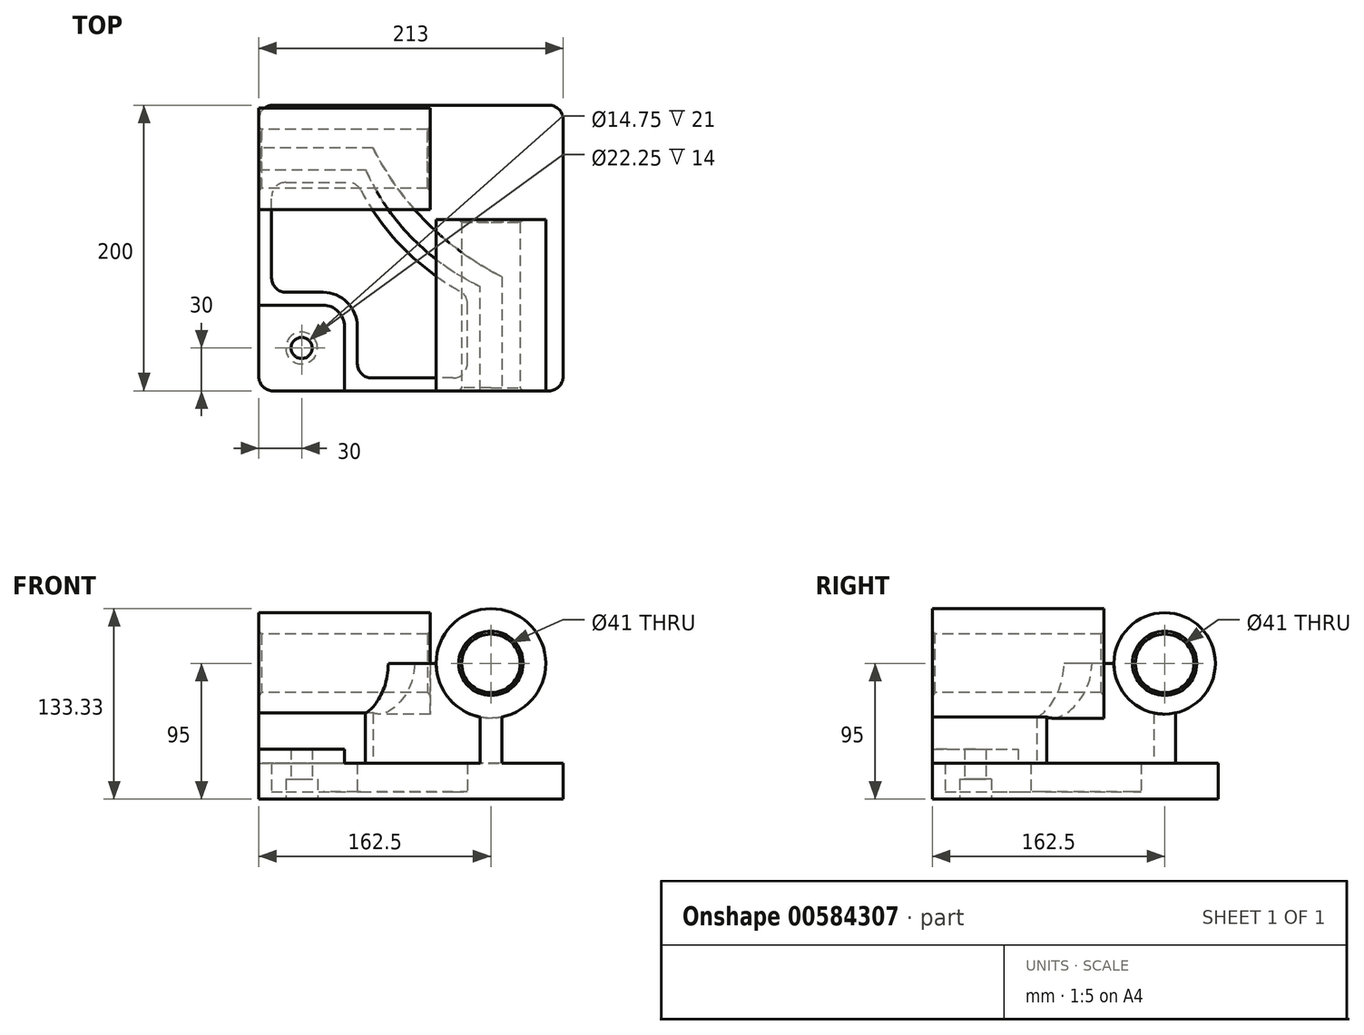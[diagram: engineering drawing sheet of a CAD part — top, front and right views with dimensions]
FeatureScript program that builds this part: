
annotation { "Feature Type Name" : "Feature", "Feature Type Description" : "" }
export const myFeature = defineFeature(function(context is Context, id is Id, definition is map)
    precondition{}
    {
        {
            var Q0;
            Q0=qCreatedBy(makeId("Top.planeOp"),FACE);
            var sketch = newSketch(context, id + "F0", { "sketchPlane" : qUnion([Q0])});
            skLineSegment(sketch, "E0", {"start": v(-96.5, 0) * mm, "end": v(96.5, 0) * mm});
            skLineSegment(sketch, "E1", {"start": v(106.5, 10) * mm, "end": v(106.5, 190) * mm});
            skLineSegment(sketch, "E2", {"start": v(96.5, 200) * mm, "end": v(-96.5, 200) * mm});
            skLineSegment(sketch, "E3", {"start": v(-106.5, 10) * mm, "end": v(-106.5, 190) * mm});
            skLineSegment(sketch, "E4", {"start": v(0, 0) * mm, "end": v(0, 200) * mm, "construction": true});
            skLineSegment(sketch, "E5", {"start": v(106.5, 100) * mm, "end": v(-106.5, 100) * mm, "construction": true});
            skPoint(sketch, "E6", {"position": v(63.5, 0) * mm});
            skPoint(sketch, "E7", {"position": v(48.5, 0) * mm});
            skLineSegment(sketch, "E8", {"start": v(48.5, 0) * mm, "end": v(48.5, 9) * mm});
            skLineSegment(sketch, "E9", {"start": v(63.5, 0) * mm, "end": v(63.5, 80) * mm});
            skPoint(sketch, "E10.visualSharp", {"position": v(106.5, 200) * mm});
            skArc(sketch, "E10.filletArc", {"start": v(106.5, 190) * mm, "mid": v(103.57, 197.07) * mm, "end": v(96.5, 200) * mm});
            skPoint(sketch, "E11.visualSharp", {"position": v(-106.5, 200) * mm});
            skArc(sketch, "E11.filletArc", {"start": v(-96.5, 200) * mm, "mid": v(-103.57, 197.07) * mm, "end": v(-106.5, 190) * mm});
            skPoint(sketch, "E12.visualSharp", {"position": v(106.5, 0) * mm});
            skArc(sketch, "E12.filletArc", {"start": v(96.5, 0) * mm, "mid": v(103.57, 2.93) * mm, "end": v(106.5, 10) * mm});
            skPoint(sketch, "E13.visualSharp", {"position": v(-106.5, 0) * mm});
            skArc(sketch, "E13.filletArc", {"start": v(-106.5, 10) * mm, "mid": v(-103.57, 2.93) * mm, "end": v(-96.5, 0) * mm});
            skPoint(sketch, "E14", {"position": v(-106.5, 155) * mm});
            skPoint(sketch, "E15", {"position": v(-106.5, 170) * mm});
            skPoint(sketch, "E16", {"position": v(-97.5, 200) * mm});
            skLineSegment(sketch, "E17", {"start": v(-106.5, 170) * mm, "end": v(-26.5, 170) * mm});
            skLineSegment(sketch, "E18", {"start": v(-46.5, 0) * mm, "end": v(-46.5, 45) * mm});
            skLineSegment(sketch, "E19", {"start": v(-61.5, 60) * mm, "end": v(-106.5, 60) * mm});
            skPoint(sketch, "E20.visualSharp", {"position": v(-46.5, 60) * mm});
            skArc(sketch, "E20.filletArc", {"start": v(-46.5, 45) * mm, "mid": v(-50.9, 55.6) * mm, "end": v(-61.5, 60) * mm});
            skLineSegment(sketch, "E21", {"start": v(-87.5, 69) * mm, "end": v(-61.5, 69) * mm});
            skLineSegment(sketch, "E22", {"start": v(-37.5, 19) * mm, "end": v(-37.5, 45) * mm});
            skPoint(sketch, "E23.visualSharp", {"position": v(-37.5, 69) * mm});
            skArc(sketch, "E23.filletArc", {"start": v(-37.5, 45) * mm, "mid": v(-44.53, 61.97) * mm, "end": v(-61.5, 69) * mm});
            skLineSegment(sketch, "E24", {"start": v(-106.5, 155) * mm, "end": v(-31.82, 155) * mm});
            skLineSegment(sketch, "E25", {"start": v(-97.5, 79) * mm, "end": v(-97.5, 136) * mm});
            skLineSegment(sketch, "E26", {"start": v(-87.5, 146) * mm, "end": v(-44.04, 146) * mm});
            skPoint(sketch, "E27.visualSharp", {"position": v(-97.5, 69) * mm});
            skArc(sketch, "E27.filletArc", {"start": v(-97.5, 79) * mm, "mid": v(-94.57, 71.93) * mm, "end": v(-87.5, 69) * mm});
            skPoint(sketch, "E28.visualSharp", {"position": v(-97.5, 146) * mm});
            skArc(sketch, "E28.filletArc", {"start": v(-87.5, 146) * mm, "mid": v(-94.57, 143.07) * mm, "end": v(-97.5, 136) * mm});
            skLineSegment(sketch, "E29", {"start": v(29.5, 9) * mm, "end": v(-27.5, 9) * mm});
            skPoint(sketch, "E30.visualSharp", {"position": v(-37.5, 9) * mm});
            skArc(sketch, "E30.filletArc", {"start": v(-37.5, 19) * mm, "mid": v(-34.57, 11.93) * mm, "end": v(-27.5, 9) * mm});
            skArc(sketch, "E31", {"start": v(-26.5, 170) * mm, "mid": v(11.24, 117.74) * mm, "end": v(63.5, 80) * mm});
            skLineSegment(sketch, "E32", {"start": v(48.5, 9) * mm, "end": v(48.5, 73.06) * mm});
            skArc(sketch, "E33", {"start": v(-31.82, 155) * mm, "mid": v(1, 106.83) * mm, "end": v(48.5, 73.06) * mm});
            skPoint(sketch, "E34", {"position": v(39.5, 9) * mm});
            skLineSegment(sketch, "E35", {"start": v(39.5, 19) * mm, "end": v(39.5, 61.05) * mm});
            skArc(sketch, "E36", {"start": v(-35.2, 140.68) * mm, "mid": v(-5.58, 100.18) * mm, "end": v(34.35, 69.8) * mm});
            skPoint(sketch, "E37.visualSharp", {"position": v(-37.9, 146) * mm});
            skArc(sketch, "E37.filletArc", {"start": v(-35.2, 140.68) * mm, "mid": v(-38.88, 144.57) * mm, "end": v(-44.04, 146) * mm});
            skPoint(sketch, "E38.visualSharp", {"position": v(39.5, 67.06) * mm});
            skArc(sketch, "E38.filletArc", {"start": v(39.5, 61.05) * mm, "mid": v(38.12, 66.13) * mm, "end": v(34.35, 69.8) * mm});
            skArc(sketch, "E39.filletArc", {"start": v(29.5, 9) * mm, "mid": v(36.57, 11.93) * mm, "end": v(39.5, 19) * mm});
            skLineSegment(sketch, "E40", {"start": v(-76.5, 0) * mm, "end": v(-76.5, 60) * mm, "construction": true});
            skLineSegment(sketch, "E41", {"start": v(-106.5, 30) * mm, "end": v(-46.5, 30) * mm, "construction": true});
            skPoint(sketch, "E42.center.orphan", {"position": v(-76.5, 30) * mm});
            skSolve(sketch);
        }
        {
            var Q0;
            {var subQ1=sQuery(id+"F0.wireOp",EDGE,"E13.filletArc");Q0=makeQuery(id+"F0.imprint","IMPRINT",FACE,{"disambiguationData":[TD([[makeQuery(id+"F0.imprint","IMPRINT",EDGE,{"derivedFrom":subQ1}),1.0]])]});}
            extrude(context, id + "F1", {"entities" : qUnion([Q0]), "depth" : 35 * mm, "offsetDistance" : 25 * mm});
        }
        {
            var Q0;
            {var subQ0=sQuery(id+"F0.wireOp",EDGE,"E8");Q0=makeQuery(id+"F0.imprint","IMPRINT",FACE,{"disambiguationData":[TD([[makeQuery(id+"F0.imprint","IMPRINT",EDGE,{"derivedFrom":subQ0}),1.0]])]});}
            extrude(context, id + "F2", {"entities" : qUnion([Q0]), "operationType" : NewBodyOperationType.ADD, "depth" : 25 * mm, "offsetDistance" : 25 * mm});
        }
        {
            var Q0;
            Q0=makeQuery(id+"F0.imprint","IMPRINT",FACE,{"disambiguationData":[TD([[makeQuery(id+"F0.imprint","IMPRINT",EDGE,{"derivedFrom":sQuery(id+"F0.wireOp",EDGE,"E21")}),1.0]])]});
            extrude(context, id + "F3", {"entities" : qUnion([Q0]), "operationType" : NewBodyOperationType.ADD, "depth" : 5 * mm, "offsetDistance" : 25 * mm});
        }
        {
            var Q0;
            {var subQ1=sQuery(id+"F0.wireOp",EDGE,"E8");Q0=makeQuery(id+"F0.imprint","IMPRINT",FACE,{"disambiguationData":[TD([[makeQuery(id+"F0.imprint","IMPRINT",EDGE,{"derivedFrom":subQ1}),-1.0]])]});}
            extrude(context, id + "F4", {"entities" : qUnion([Q0]), "operationType" : NewBodyOperationType.ADD, "depth" : 95 * mm, "offsetDistance" : 25 * mm});
        }
        {
            var Q0;
            Q0=sQuery(id+"F0.wireOp",VERTEX,"E42.center.orphan");
            var Q1;
            Q1=makeQuery(id+"F1.opExtrude","SWEPT_BODY",BODY,{"disambiguationData":[OSD([sQuery(id+"F0.wireOp",EDGE,"E0"),sQuery(id+"F0.wireOp",EDGE,"E3"),sQuery(id+"F0.wireOp",EDGE,"E13.filletArc"),sQuery(id+"F0.wireOp",EDGE,"E18"),sQuery(id+"F0.wireOp",EDGE,"E19"),sQuery(id+"F0.wireOp",EDGE,"E20.filletArc")])]});
            hole(context, id + "F5", {"style" : HoleStyle.C_BORE, "endStyle" : HoleEndStyle.THROUGH, "oppositeDirection" : true, "standardTappedOrClearance" : lookupTablePath({ "standard" : "ISO", "fit" : "Close", "size" : "M14", "type" : "Clearance" }), "standardBlindInLast" : lookupTablePath({ "fit" : "Close", "standard" : "ISO", "size" : "M14", "type" : "Clearance" }), "holeDiameter" : 14.75 * mm, "cBoreDiameter" : 22.25 * mm, "cBoreDepth" : 14 * mm, "majorDiameter" : 5 * mm, "isTappedThrough" : true, "tappedDepth" : 12 * mm, "tapClearance" : 3, "locations" : qUnion([Q0]), "scope" : qUnion([Q1])});
        }
        {
            var Q0;
            Q0=makeQuery(id+"F0.imprint","IMPRINT",FACE,{"disambiguationData":[TD([[makeQuery(id+"F0.imprint","IMPRINT",EDGE,{"derivedFrom":sQuery(id+"F0.wireOp",EDGE,"E1")}),1.0]])]});
            extrude(context, id + "F6", {"entities" : qUnion([Q0]), "operationType" : NewBodyOperationType.ADD, "depth" : 25 * mm, "offsetDistance" : 25 * mm});
        }
        {
            var Q0;
            {var subQ0=sQuery(id+"F0.wireOp",EDGE,"E0");Q0=makeQuery(id+"F6.boolean.opBoolean","MERGE",FACE,{"derivedFrom":[makeQuery(id+"F4.boolean.opBoolean","MERGE",FACE,{"derivedFrom":[makeQuery(id+"F2.boolean.opBoolean","MERGE",FACE,{"derivedFrom":[makeQuery(id+"F1.opExtrude","SWEPT_FACE",FACE,{"disambiguationData":[OSD([subQ0])]}),makeQuery(id+"F2.opExtrude","SWEPT_FACE",FACE,{"disambiguationData":[OSD([subQ0])]})]}),makeQuery(id+"F4.opExtrude","SWEPT_FACE",FACE,{"disambiguationData":[OSD([subQ0])]})]}),makeQuery(id+"F6.opExtrude","SWEPT_FACE",FACE,{"disambiguationData":[OSD([subQ0])]})]});}
            var sketch = newSketch(context, id + "F7", { "sketchPlane" : qUnion([Q0])});
            skLineSegment(sketch, "E43.0", {"start": v(48.5, 95) * mm, "end": v(63.5, 95) * mm});
            skLineSegment(sketch, "E44", {"start": v(56, 95) * mm, "end": v(56, 0) * mm, "construction": true});
            skCircle(sketch, "E45", {"center": v(56, 95) * mm, "radius": 20.5 * mm});
            skCircle(sketch, "E46", {"center": v(56, 95) * mm, "radius": 38.33 * mm});
            skSolve(sketch);
        }
        {
            var Q0;
            {var subQ0=sQuery(id+"F7.wireOp",EDGE,"E43.0");Q0=makeQuery(id+"F7.imprint","IMPRINT",FACE,{"disambiguationData":[TD([[makeQuery(id+"F7.imprint","IMPRINT",EDGE,{"derivedFrom":subQ0}),1.0]])]});}
            var Q1;
            {var subQ0=sQuery(id+"F7.wireOp",EDGE,"E43.0");Q1=makeQuery(id+"F7.imprint","IMPRINT",FACE,{"disambiguationData":[TD([[makeQuery(id+"F7.imprint","IMPRINT",EDGE,{"derivedFrom":subQ0}),-1.0]])]});}
            extrude(context, id + "F8", {"entities" : qUnion([Q0, Q1]), "operationType" : NewBodyOperationType.REMOVE, "oppositeDirection" : true, "depth" : 120 * mm, "offsetDistance" : 25 * mm});
        }
        {
            var Q0;
            {var subQ0=sQuery(id+"F7.wireOp",EDGE,"E45");var subQ1=sQuery(id+"F0.wireOp",EDGE,"E0");var subQ2=makeQuery(id+"F4.opExtrude","SWEPT_EDGE",EDGE,{"disambiguationData":[OSD([subQ1,sQuery(id+"F0.wireOp",EDGE,"E8")])]});var subQ3=makeQuery(id+"F7.imprint","INTERSECT",VERTEX,{"derivedFrom":[subQ2,subQ0]});Q0=makeQuery(id+"F7.imprint","IMPRINT",FACE,{"disambiguationData":[TD([[makeQuery(id+"F7.imprint","IMPRINT",EDGE,{"disambiguationData":[TD([[subQ3,1.0]])],"derivedFrom":subQ0}),-1.0]])]});}
            var Q1;
            {var subQ0=sQuery(id+"F7.wireOp",EDGE,"E45");var subQ1=sQuery(id+"F0.wireOp",EDGE,"E0");var subQ2=makeQuery(id+"F4.opExtrude","SWEPT_EDGE",EDGE,{"disambiguationData":[OSD([subQ1,sQuery(id+"F0.wireOp",EDGE,"E8")])]});var subQ3=makeQuery(id+"F7.imprint","INTERSECT",VERTEX,{"derivedFrom":[subQ2,subQ0]});Q1=makeQuery(id+"F7.imprint","IMPRINT",FACE,{"disambiguationData":[TD([[makeQuery(id+"F7.imprint","IMPRINT",EDGE,{"disambiguationData":[TD([[subQ3,-1.0]])],"derivedFrom":subQ0}),-1.0]])]});}
            extrude(context, id + "F9", {"entities" : qUnion([Q0, Q1]), "operationType" : NewBodyOperationType.ADD, "oppositeDirection" : true, "depth" : 120 * mm, "offsetDistance" : 25 * mm});
        }
        {
            var Q0;
            {var subQ0=sQuery(id+"F0.wireOp",EDGE,"E3");Q0=makeQuery(id+"F6.boolean.opBoolean","MERGE",FACE,{"derivedFrom":[makeQuery(id+"F4.boolean.opBoolean","MERGE",FACE,{"derivedFrom":[makeQuery(id+"F2.boolean.opBoolean","MERGE",FACE,{"derivedFrom":[makeQuery(id+"F1.opExtrude","SWEPT_FACE",FACE,{"disambiguationData":[OSD([subQ0])]}),makeQuery(id+"F2.opExtrude","SWEPT_FACE",FACE,{"disambiguationData":[OSD([subQ0])]})]}),makeQuery(id+"F4.opExtrude","SWEPT_FACE",FACE,{"disambiguationData":[OSD([subQ0])]})]}),makeQuery(id+"F6.opExtrude","SWEPT_FACE",FACE,{"disambiguationData":[OSD([subQ0])]})]});}
            var sketch = newSketch(context, id + "F10", { "sketchPlane" : qUnion([Q0])});
            skLineSegment(sketch, "E47.0", {"start": v(-155, 95) * mm, "end": v(-170, 95) * mm});
            skLineSegment(sketch, "E48", {"start": v(-162.5, 95) * mm, "end": v(-162.5, 0) * mm, "construction": true});
            skCircle(sketch, "E49", {"center": v(-162.5, 95) * mm, "radius": 20.5 * mm});
            skCircle(sketch, "E50", {"center": v(-162.5, 95) * mm, "radius": 35.5 * mm});
            skSolve(sketch);
        }
        {
            var Q0;
            {var subQ0=sQuery(id+"F10.wireOp",EDGE,"E47.0");Q0=makeQuery(id+"F10.imprint","IMPRINT",FACE,{"disambiguationData":[TD([[makeQuery(id+"F10.imprint","IMPRINT",EDGE,{"derivedFrom":subQ0}),-1.0]])]});}
            var Q1;
            {var subQ0=sQuery(id+"F10.wireOp",EDGE,"E47.0");Q1=makeQuery(id+"F10.imprint","IMPRINT",FACE,{"disambiguationData":[TD([[makeQuery(id+"F10.imprint","IMPRINT",EDGE,{"derivedFrom":subQ0}),1.0]])]});}
            extrude(context, id + "F11", {"entities" : qUnion([Q0, Q1]), "operationType" : NewBodyOperationType.REMOVE, "oppositeDirection" : true, "depth" : 120 * mm, "offsetDistance" : 25 * mm});
        }
        {
            var Q0;
            {var subQ0=sQuery(id+"F10.wireOp",EDGE,"E49");var subQ1=sQuery(id+"F0.wireOp",EDGE,"E3");var subQ2=makeQuery(id+"F4.opExtrude","SWEPT_EDGE",EDGE,{"disambiguationData":[OSD([subQ1,sQuery(id+"F0.wireOp",EDGE,"E24")])]});var subQ3=makeQuery(id+"F10.imprint","INTERSECT",VERTEX,{"derivedFrom":[subQ2,subQ0]});Q0=makeQuery(id+"F10.imprint","IMPRINT",FACE,{"disambiguationData":[TD([[makeQuery(id+"F10.imprint","IMPRINT",EDGE,{"disambiguationData":[TD([[subQ3,-1.0]])],"derivedFrom":subQ0}),-1.0]])]});}
            var Q1;
            {var subQ0=sQuery(id+"F10.wireOp",EDGE,"E49");var subQ1=sQuery(id+"F0.wireOp",EDGE,"E3");var subQ2=makeQuery(id+"F4.opExtrude","SWEPT_EDGE",EDGE,{"disambiguationData":[OSD([subQ1,sQuery(id+"F0.wireOp",EDGE,"E24")])]});var subQ3=makeQuery(id+"F10.imprint","INTERSECT",VERTEX,{"derivedFrom":[subQ2,subQ0]});Q1=makeQuery(id+"F10.imprint","IMPRINT",FACE,{"disambiguationData":[TD([[makeQuery(id+"F10.imprint","IMPRINT",EDGE,{"disambiguationData":[TD([[subQ3,1.0]])],"derivedFrom":subQ0}),-1.0]])]});}
            extrude(context, id + "F12", {"entities" : qUnion([Q0, Q1]), "operationType" : NewBodyOperationType.ADD, "oppositeDirection" : true, "depth" : 120 * mm, "offsetDistance" : 25 * mm});
        }
        {
            var Q0;
            {var subQ0=sQuery(id+"F7.wireOp",EDGE,"E45");Q0=makeQuery(id+"F9.boolean.opBoolean","MERGE",EDGE,{"derivedFrom":[makeQuery(id+"F8.boolean.opBoolean","COPY",EDGE,{"derivedFrom":makeQuery(id+"F8.opExtrude","CAP_EDGE",EDGE,{"disambiguationData":[OSD([subQ0])],"isStart":true})}),makeQuery(id+"F9.opExtrude","CAP_EDGE",EDGE,{"disambiguationData":[OSD([subQ0])],"isStart":true})]});}
            var Q1;
            Q1=makeQuery(id+"F9.opExtrude","CAP_EDGE",EDGE,{"disambiguationData":[OSD([sQuery(id+"F7.wireOp",EDGE,"E45")])],"isStart":false});
            var Q2;
            Q2=makeQuery(id+"F12.opExtrude","CAP_EDGE",EDGE,{"disambiguationData":[OSD([sQuery(id+"F10.wireOp",EDGE,"E49")])],"isStart":false});
            var Q3;
            {var subQ0=sQuery(id+"F10.wireOp",EDGE,"E49");Q3=makeQuery(id+"F12.boolean.opBoolean","MERGE",EDGE,{"derivedFrom":[makeQuery(id+"F11.boolean.opBoolean","COPY",EDGE,{"derivedFrom":makeQuery(id+"F11.opExtrude","CAP_EDGE",EDGE,{"disambiguationData":[OSD([subQ0])],"isStart":true})}),makeQuery(id+"F12.opExtrude","CAP_EDGE",EDGE,{"disambiguationData":[OSD([subQ0])],"isStart":true})]});}
            chamfer(context, id + "F13", {"entities" : qUnion([Q0, Q1, Q2, Q3]), "width" : 2 * mm, "tangentPropagation" : true});
        }
    });
